# Revit family: Shower_Base-American_Standard-60x30-A8001L_Series
name_source: partatom
category: Plumbing Fixtures
revit_build: Autodesk Revit 2018 (Build: 20170223_1515(x64)
units: mm (PartAtom-declared; Revit-internal decimal feet)

## family parameters
Always vertical = No
Cut with Voids When Loaded = No
OmniClass Number = 23.45.05.14.17
OmniClass Title = Showers
Part Type = Normal
Room Calculation Point = No
Round Connector Dimension = Use Diameter
Shared = Yes
Work Plane-Based = Yes

## types (2) — shared parameters
Assembly Code = D2010710
CW Connection = No
CWFU = 3
Clearance Between Studding = 0"
Default Elevation = 2 1/2"
Description = Studio 60x30 Acrylic Shower Base. American Standard acrylic shower bases are stylishly designed with an easy to step over, low threshold. Designed to provide a minimalist look with clean simple lines, these sleek and sophisticated shower floors look great in any bathroom. Our shower bases are made of durable acrylic construction with fiberglass reinforcement, built to last.
Drain Length = 14 1/2"
Finish = Acrylic-American_Standard-020-White
HW Connection = No
HWFU = 3
Height = 3 1/2"
IAPMO Compliance = CSA B45.5 / IAPMO Z124, IAPMO R&T cUPC
Installation Type = Floor Mounted
Length = 30"
Manufacturer = American Standard
Material = Acrylic-American_Standard-020-White
Price = Prices may vary. Please consult Manufacturer Representative for most up-to-date price list.
Product Documentation Link = https://www.americanstandard-us.com
Product Page URL = https://www.americanstandard-us.com
Revised Date = 03/25/2021
Strainer Finish = Metal-American_Standard-Stainless_Steel-Brushed
URL = https://www.americanstandard-us.com
Vent Connection = No
WFU = 4
Warranty Information = Limited Lifetime Warranty
Waste Connection = Yes
Waste Connection Diameter = 3 1/4"
Waste Connection Radius = 1 5/8"
Width = 60"

## per-type parameters (varying)
| type | Drain Location | Left Side Drain | Right Side Drain |
| A8001L.LHO | 8" | Yes | No |
| A8001L.RHO | 52" | No | Yes |

note: column(s) folded — value = type name in every type: Model

## geometry (parser evidence)
native form markers: Sweep x2
no freeform markers — native parametric forms only
